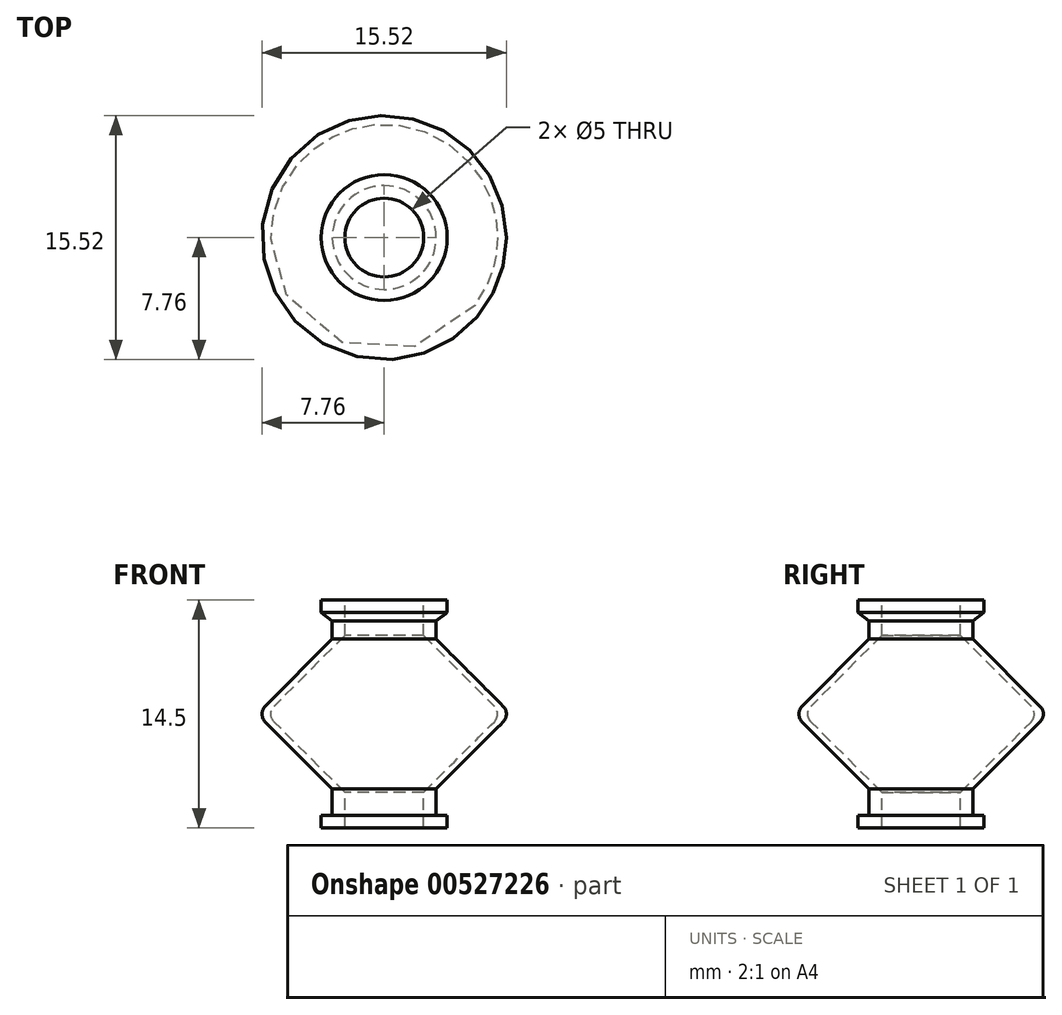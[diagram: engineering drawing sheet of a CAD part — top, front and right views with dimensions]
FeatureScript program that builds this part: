
annotation { "Feature Type Name" : "Feature", "Feature Type Description" : "" }
export const myFeature = defineFeature(function(context is Context, id is Id, definition is map)
    precondition{}
    {
        {
            var Q0;
            Q0=qCreatedBy(makeId("Front.planeOp"),FACE);
            var sketch = newSketch(context, id + "F0", { "sketchPlane" : qUnion([Q0])});
            skLineSegment(sketch, "E0", {"start": v(-2.5, 7.25) * mm, "end": v(-4, 7.25) * mm});
            skLineSegment(sketch, "E1", {"start": v(-3.3, 5.91) * mm, "end": v(-3.3, 4.75) * mm});
            skLineSegment(sketch, "E2", {"start": v(-2.5, 7.25) * mm, "end": v(-2.5, 4.98) * mm});
            skLineSegment(sketch, "E3.MirrorCS", {"start": v(-3.3, -4.75) * mm, "end": v(-7.56, -0.5) * mm});
            skLineSegment(sketch, "E4.MirrorCS", {"start": v(-3.3, -6.45) * mm, "end": v(-3.3, -4.75) * mm});
            skLineSegment(sketch, "E5.MirrorCS", {"start": v(-4, -6.45) * mm, "end": v(-3.3, -6.45) * mm});
            skLineSegment(sketch, "E6.MirrorCS", {"start": v(-4, -7.25) * mm, "end": v(-4, -6.45) * mm});
            skLineSegment(sketch, "E7.MirrorCS", {"start": v(-2.5, -7.25) * mm, "end": v(-4, -7.25) * mm});
            skLineSegment(sketch, "E8.MirrorCS", {"start": v(-2.5, -7.25) * mm, "end": v(-2.5, -4.98) * mm});
            skLineSegment(sketch, "E9", {"start": v(0, 8.81) * mm, "end": v(0, -10.41) * mm, "construction": true});
            skLineSegment(sketch, "E10.MirrorCS", {"start": v(-3.3, 4.75) * mm, "end": v(-7.56, 0.5) * mm});
            skLineSegment(sketch, "E11", {"start": v(-6.99, 0.5) * mm, "end": v(-2.5, 4.98) * mm});
            skArc(sketch, "E12", {"start": v(-7.56, 0.5) * mm, "mid": v(-7.76, 0) * mm, "end": v(-7.56, -0.5) * mm});
            skArc(sketch, "E13", {"start": v(-6.99, 0.5) * mm, "mid": v(-7.2, 0) * mm, "end": v(-6.99, -0.5) * mm});
            skLineSegment(sketch, "E14.MirrorCS", {"start": v(-6.99, -0.5) * mm, "end": v(-2.5, -4.98) * mm});
            skLineSegment(sketch, "E15", {"start": v(-4, 6.45) * mm, "end": v(-3.3, 5.91) * mm});
            skLineSegment(sketch, "E16", {"start": v(-4, 7.25) * mm, "end": v(-4, 6.45) * mm});
            skSolve(sketch);
        }
        {
            var Q0;
            Q0=qSketchRegion(id+"F0",true);
            var Q1;
            Q1=sQuery(id+"F0.wireOp",EDGE,"E9");
            revolve(context, id + "F1", {"entities" : qUnion([Q0]), "axis" : qUnion([Q1]), "revolveType" : RevolveType.FULL});
        }
    });
